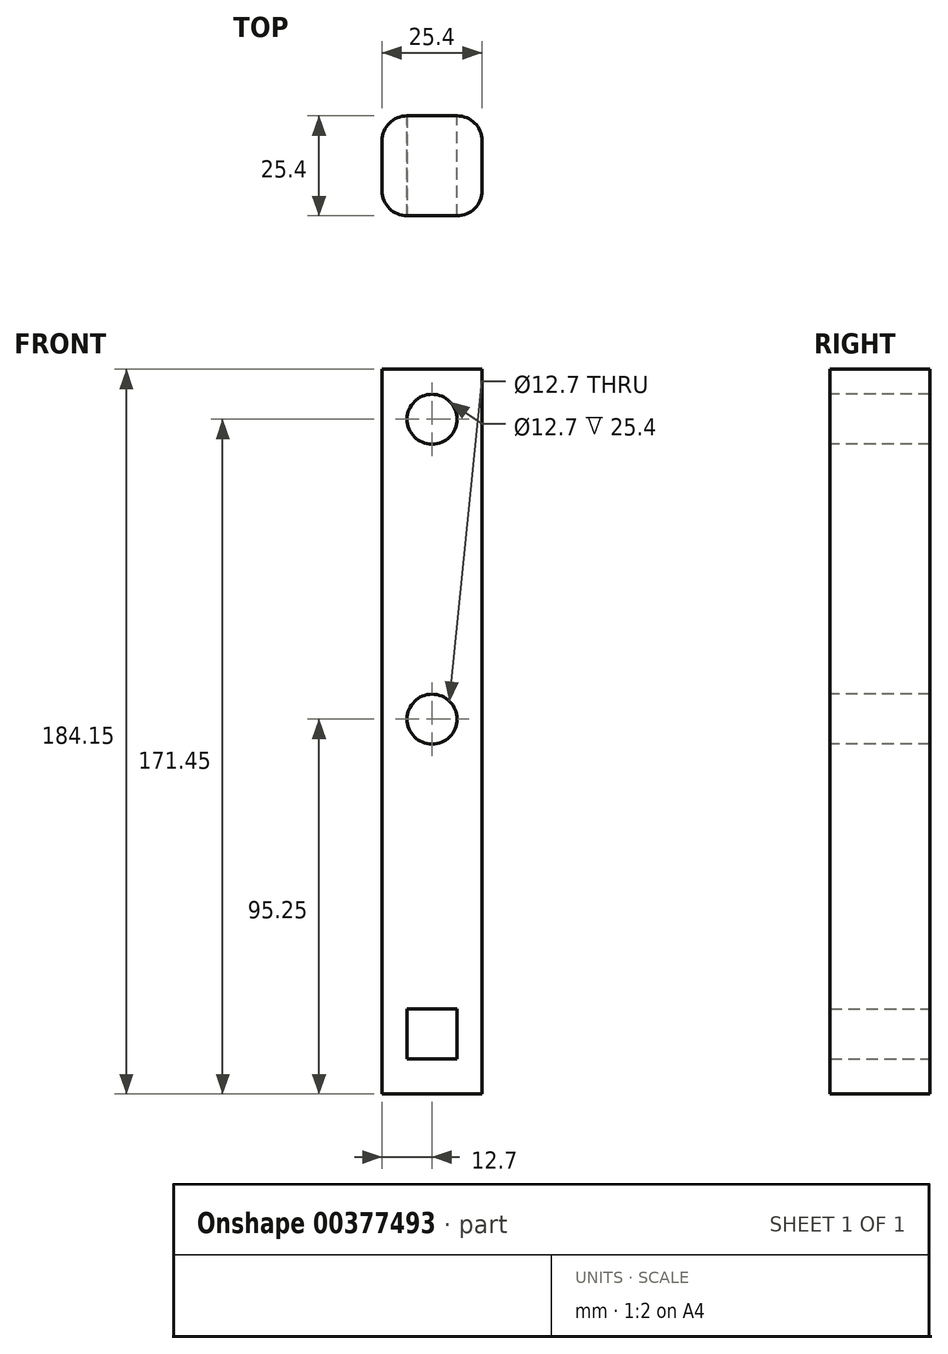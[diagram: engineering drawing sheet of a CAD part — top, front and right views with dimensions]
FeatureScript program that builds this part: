
annotation { "Feature Type Name" : "Feature", "Feature Type Description" : "" }
export const myFeature = defineFeature(function(context is Context, id is Id, definition is map)
    precondition{}
    {
        {
            var Q0;
            Q0=qCreatedBy(makeId("Front.planeOp"),FACE);
            var sketch = newSketch(context, id + "F0", { "sketchPlane" : qUnion([Q0])});
            skLineSegment(sketch, "E0", {"start": v(0, -32) * mm, "end": v(-12.7, -32) * mm});
            skLineSegment(sketch, "E1", {"start": v(-12.7, -32) * mm, "end": v(-12.7, 69.6) * mm});
            skLineSegment(sketch, "E2.MirrorCS", {"start": v(0, -32) * mm, "end": v(12.7, -32) * mm});
            skLineSegment(sketch, "E3.MirrorCS", {"start": v(12.7, -32) * mm, "end": v(12.7, 69.6) * mm});
            skLineSegment(sketch, "E4", {"start": v(12.7, 69.6) * mm, "end": v(-12.7, 69.6) * mm});
            skSolve(sketch);
        }
        {
            var Q0;
            Q0 = qSketchRegion(id + "F0", true);
            extrude(context, id + "F1", {"entities" : qUnion([Q0]), "depth" : 25.4 * mm});
        }
        {
            var Q0;
            Q0=makeQuery(id+"F1.opExtrude","CAP_FACE",FACE,{"disambiguationData":[OSD([sQuery(id+"F0.wireOp",EDGE,"E0"),sQuery(id+"F0.wireOp",EDGE,"E1"),sQuery(id+"F0.wireOp",EDGE,"E2.MirrorCS"),sQuery(id+"F0.wireOp",EDGE,"E3.MirrorCS"),sQuery(id+"F0.wireOp",EDGE,"E4")])],"isStart":false});
            var sketch = newSketch(context, id + "F2", { "sketchPlane" : qUnion([Q0])});
            skLineSegment(sketch, "E5", {"start": v(0, 69.6) * mm, "end": v(0, -32) * mm});
            skLineSegment(sketch, "E6", {"start": v(0, -32) * mm, "end": v(0, 18.8) * mm});
            skLineSegment(sketch, "E7", {"start": v(0, 18.8) * mm, "end": v(0, -6.6) * mm});
            skLineSegment(sketch, "E8", {"start": v(0, -6.6) * mm, "end": v(0, 18.8) * mm});
            skLineSegment(sketch, "E9", {"start": v(0, 18.8) * mm, "end": v(0, 69.6) * mm});
            skLineSegment(sketch, "E10", {"start": v(0, 69.6) * mm, "end": v(0, 44.2) * mm});
            skLineSegment(sketch, "E11", {"start": v(0, 69.6) * mm, "end": v(0, 56.9) * mm});
            skLineSegment(sketch, "E12", {"start": v(0, -32) * mm, "end": v(0, -6.6) * mm});
            skLineSegment(sketch, "E13", {"start": v(0, -6.6) * mm, "end": v(0, -19.3) * mm});
            skSolve(sketch);
        }
        {
            var Q0;
            Q0=sQuery(id+"F2.wireOp",VERTEX,"E11.end");
            var Q1;
            Q1=sQuery(id+"F2.wireOp",VERTEX,"E13.end");
            var Q2;
            Q2=makeQuery(id+"F1.opExtrude","SWEPT_BODY",BODY,{"disambiguationData":[OSD([sQuery(id+"F0.wireOp",EDGE,"E0"),sQuery(id+"F0.wireOp",EDGE,"E1"),sQuery(id+"F0.wireOp",EDGE,"E2.MirrorCS"),sQuery(id+"F0.wireOp",EDGE,"E3.MirrorCS"),sQuery(id+"F0.wireOp",EDGE,"E4")])]});
            hole(context, id + "F3", {"style" : HoleStyle.SIMPLE, "endStyle" : HoleEndStyle.BLIND, "holeDiameter" : 12.7 * mm, "holeDepth" : 254 * mm, "tappedDepth" : 12.7 * mm, "tapClearance" : 3, "locations" : qUnion([Q0, Q1]), "scope" : qUnion([Q2])});
        }
        {
            var Q0;
            Q0=makeQuery(id+"F1.opExtrude","CAP_FACE",FACE,{"disambiguationData":[OSD([sQuery(id+"F0.wireOp",EDGE,"E0"),sQuery(id+"F0.wireOp",EDGE,"E1"),sQuery(id+"F0.wireOp",EDGE,"E2.MirrorCS"),sQuery(id+"F0.wireOp",EDGE,"E3.MirrorCS"),sQuery(id+"F0.wireOp",EDGE,"E4")])],"isStart":false});
            var sketch = newSketch(context, id + "F4", { "sketchPlane" : qUnion([Q0])});
            skLineSegment(sketch, "E14", {"start": v(12.7, -32) * mm, "end": v(12.7, -114.56) * mm});
            skLineSegment(sketch, "E15", {"start": v(-12.7, -32) * mm, "end": v(-12.7, -114.56) * mm});
            skLineSegment(sketch, "E16", {"start": v(12.7, -114.56) * mm, "end": v(-12.7, -114.56) * mm});
            skSolve(sketch);
        }
        {
            var Q0;
            Q0=makeQuery(id+"F4.imprint","IMPRINT",FACE,{"disambiguationData":[TD([[makeQuery(id+"F4.imprint","IMPRINT",EDGE,{"derivedFrom":sQuery(id+"F4.wireOp",EDGE,"E14")}),-1.0]])]});
            extrude(context, id + "F5", {"entities" : qUnion([Q0]), "operationType" : NewBodyOperationType.ADD, "depth" : -25.4 * mm});
        }
        {
            var Q0;
            {var subQ0=sQuery(id+"F0.wireOp",EDGE,"E2.MirrorCS");var subQ1=sQuery(id+"F0.wireOp",EDGE,"E0");Q0=makeQuery(id+"F5.boolean.opBoolean","MERGE",FACE,{"derivedFrom":[makeQuery(id+"F1.opExtrude","CAP_FACE",FACE,{"disambiguationData":[OSD([subQ1,sQuery(id+"F0.wireOp",EDGE,"E1"),subQ0,sQuery(id+"F0.wireOp",EDGE,"E3.MirrorCS"),sQuery(id+"F0.wireOp",EDGE,"E4")])],"isStart":true}),makeQuery(id+"F5.opExtrude","CAP_FACE",FACE,{"disambiguationData":[OSD([subQ1,subQ0,sQuery(id+"F4.wireOp",EDGE,"E14"),sQuery(id+"F4.wireOp",EDGE,"E15"),sQuery(id+"F4.wireOp",EDGE,"E16")])],"isStart":false})]});}
            var sketch = newSketch(context, id + "F6", { "sketchPlane" : qUnion([Q0])});
            skLineSegment(sketch, "E17", {"start": v(0, -114.56) * mm, "end": v(0, -99.32) * mm});
            skLineSegment(sketch, "E18.bottom", {"start": v(6.35, -105.67) * mm, "end": v(-6.35, -105.67) * mm});
            skLineSegment(sketch, "E18.top", {"start": v(6.35, -92.97) * mm, "end": v(-6.35, -92.97) * mm});
            skLineSegment(sketch, "E18.left", {"start": v(6.35, -105.67) * mm, "end": v(6.35, -92.97) * mm});
            skLineSegment(sketch, "E18.right", {"start": v(-6.35, -105.67) * mm, "end": v(-6.35, -92.97) * mm});
            skPoint(sketch, "E18.middle", {"position": v(0, -99.32) * mm});
            skSolve(sketch);
        }
        {
            var Q0;
            Q0 = qSketchRegion(id + "F6", true);
            extrude(context, id + "F7", {"entities" : qUnion([Q0]), "operationType" : NewBodyOperationType.REMOVE, "oppositeDirection" : true, "depth" : 25.4 * mm});
        }
        {
            var Q0;
            Q0=makeQuery(id+"F5.boolean.opBoolean","MERGE",EDGE,{"derivedFrom":[makeQuery(id+"F1.opExtrude","CAP_EDGE",EDGE,{"disambiguationData":[OSD([sQuery(id+"F0.wireOp",EDGE,"E3.MirrorCS")])],"isStart":true}),makeQuery(id+"F5.opExtrude","CAP_EDGE",EDGE,{"disambiguationData":[OSD([sQuery(id+"F4.wireOp",EDGE,"E14")])],"isStart":false})]});
            var Q1;
            Q1=makeQuery(id+"F5.boolean.opBoolean","MERGE",EDGE,{"derivedFrom":[makeQuery(id+"F1.opExtrude","CAP_EDGE",EDGE,{"disambiguationData":[OSD([sQuery(id+"F0.wireOp",EDGE,"E1")])],"isStart":true}),makeQuery(id+"F5.opExtrude","CAP_EDGE",EDGE,{"disambiguationData":[OSD([sQuery(id+"F4.wireOp",EDGE,"E15")])],"isStart":false})]});
            var Q2;
            Q2=makeQuery(id+"F5.boolean.opBoolean","MERGE",EDGE,{"derivedFrom":[makeQuery(id+"F1.opExtrude","CAP_EDGE",EDGE,{"disambiguationData":[OSD([sQuery(id+"F0.wireOp",EDGE,"E1")])],"isStart":false}),makeQuery(id+"F5.opExtrude","CAP_EDGE",EDGE,{"disambiguationData":[OSD([sQuery(id+"F4.wireOp",EDGE,"E15")])],"isStart":true})]});
            var Q3;
            Q3=makeQuery(id+"F5.boolean.opBoolean","MERGE",EDGE,{"derivedFrom":[makeQuery(id+"F1.opExtrude","CAP_EDGE",EDGE,{"disambiguationData":[OSD([sQuery(id+"F0.wireOp",EDGE,"E3.MirrorCS")])],"isStart":false}),makeQuery(id+"F5.opExtrude","CAP_EDGE",EDGE,{"disambiguationData":[OSD([sQuery(id+"F4.wireOp",EDGE,"E14")])],"isStart":true})]});
            fillet(context, id + "F8", {"entities" : qUnion([Q0, Q1, Q2, Q3]), "radius" : 6.35 * mm, "tangentPropagation" : true, "allowEdgeOverflow" : false});
        }
    });
